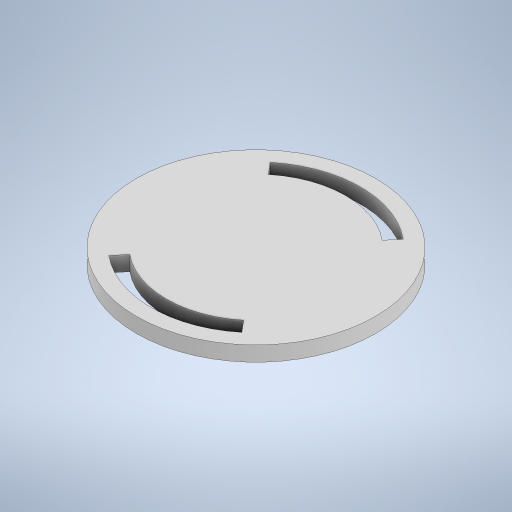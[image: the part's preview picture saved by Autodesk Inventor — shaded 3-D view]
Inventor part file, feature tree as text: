
AUTODESK INVENTOR PART (.ipt)
format: ipt  version: 2023 (Build 270158000, 158)  size: 270,336 bytes
history: native  units: in
note: dims shown in document units (in); Inventor stores cm internally (conversion verified against a paired STEP export)
features: extrude x3, sketch x2, plane x1, mirror x1
ambient origin geometry x8: Origin, YZ Plane, XZ Plane, XY Plane, X Axis, Y Axis, Z Axis, Center Point
bodies: Solid1 (feature_tree)
feature tree (7):
  extrude  "Extrusion1"  Depth=0.1969in TaperAngle=0.0deg
  extrude  "Extrusion5"  Depth=0.3937in
  extrude  "Extrusion7"  Depth=0.1575in TaperAngle=0.0deg
  plane  "Work Plane1"
  mirror  "Mirror1"
  sketch  "Sketch1"  dims[d0=3.1496in d1=0.1969in d2=0.0in]
  sketch  "Sketch8"  dims[d19=0.9843in d20=0.7874in d22=0.1575in d23=0.0in d46=0.9843in d47=180.0deg d48=0.7874in d53=0.1969in d54=0.1969in d55=120.0deg d56=0.3937in d57=0.0in d58=0.1181in d60=0.8933in d10=0.0197in d11=0.0344in d12=0.0197in d13=0.0344in d59=0.0344in]
